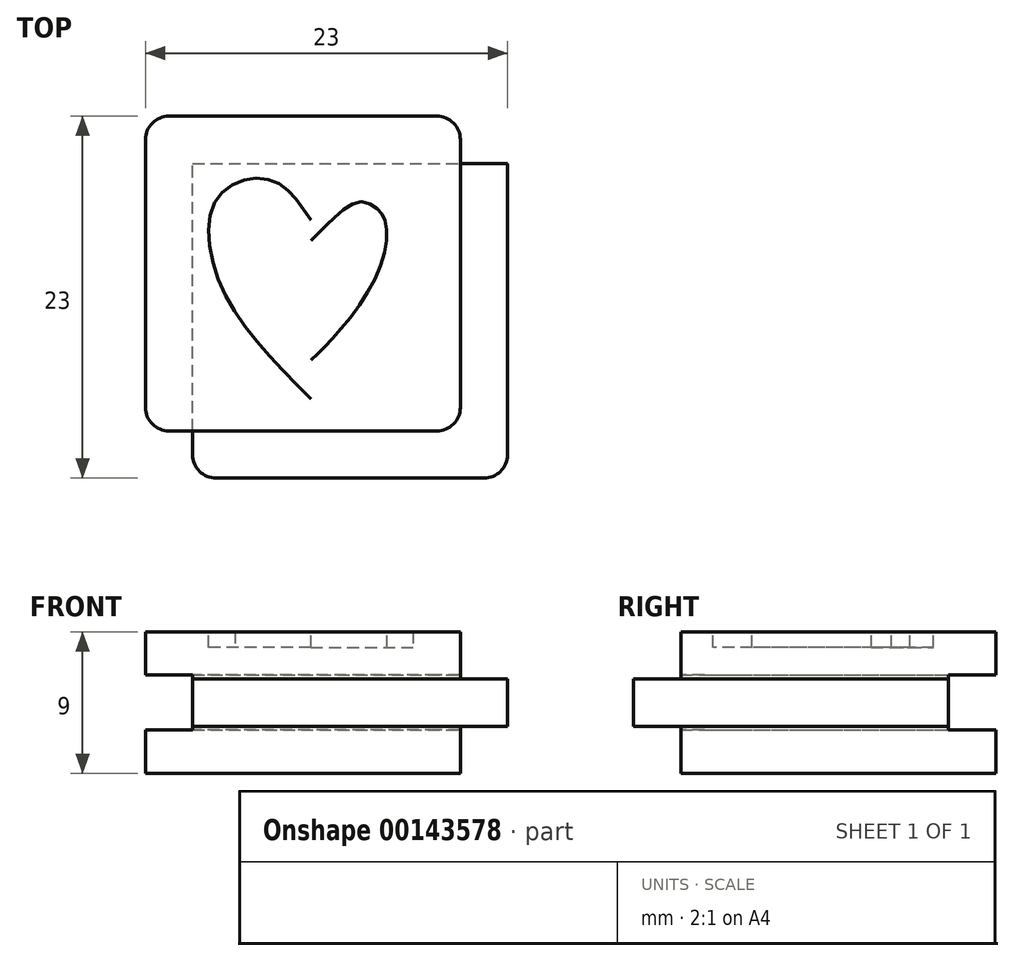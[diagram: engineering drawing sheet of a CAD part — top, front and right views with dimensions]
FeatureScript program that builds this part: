
annotation { "Feature Type Name" : "Feature", "Feature Type Description" : "" }
export const myFeature = defineFeature(function(context is Context, id is Id, definition is map)
    precondition{}
    {
        {
            var Q0;
            Q0=qCreatedBy(makeId("Front.planeOp"),FACE);
            var sketch = newSketch(context, id + "F0", { "sketchPlane" : qUnion([Q0])});
            skLineSegment(sketch, "E0.bottom", {"start": v(10, 4.5) * mm, "end": v(-10, 4.5) * mm});
            skLineSegment(sketch, "E0.top", {"start": v(10, -4.5) * mm, "end": v(-10, -4.5) * mm});
            skLineSegment(sketch, "E0.left", {"start": v(10, 4.5) * mm, "end": v(10, -4.5) * mm});
            skLineSegment(sketch, "E0.right", {"start": v(-10, 4.5) * mm, "end": v(-10, -4.5) * mm});
            skPoint(sketch, "E0.middle", {"position": v(0, 0) * mm});
            skLineSegment(sketch, "E1.bottom", {"start": v(13, 1.5) * mm, "end": v(7, 1.5) * mm});
            skLineSegment(sketch, "E1.top", {"start": v(13, -1.5) * mm, "end": v(7, -1.5) * mm});
            skLineSegment(sketch, "E1.left", {"start": v(13, 1.5) * mm, "end": v(13, -1.5) * mm});
            skLineSegment(sketch, "E1.right", {"start": v(7, 1.5) * mm, "end": v(7, -1.5) * mm});
            skPoint(sketch, "E1.middle", {"position": v(10, 0) * mm});
            skLineSegment(sketch, "E2.bottom", {"start": v(7, 1.5) * mm, "end": v(-7, 1.5) * mm});
            skLineSegment(sketch, "E2.top", {"start": v(7, -1.5) * mm, "end": v(-7, -1.5) * mm});
            skLineSegment(sketch, "E2.right", {"start": v(-7, 1.5) * mm, "end": v(-7, -1.5) * mm});
            skLineSegment(sketch, "E3.bottom", {"start": v(-7, -1.5) * mm, "end": v(-10, -1.5) * mm});
            skLineSegment(sketch, "E3.top", {"start": v(-7, 1.5) * mm, "end": v(-10, 1.5) * mm});
            skLineSegment(sketch, "E3.left", {"start": v(-7, -1.5) * mm, "end": v(-7, 1.5) * mm});
            skLineSegment(sketch, "E3.right", {"start": v(-10, -1.5) * mm, "end": v(-10, 1.5) * mm});
            skSolve(sketch);
        }
        {
            var Q0;
            {var subQ5=sQuery(id+"F0.wireOp",EDGE,"E0.bottom");Q0=makeQuery(id+"F0.imprint","IMPRINT",FACE,{"disambiguationData":[TD([[makeQuery(id+"F0.imprint","IMPRINT",EDGE,{"derivedFrom":subQ5}),1.0]])]});}
            var Q1;
            Q1=makeQuery(id+"F0.imprint","IMPRINT",FACE,{"disambiguationData":[TD([[makeQuery(id+"F0.imprint","IMPRINT",EDGE,{"derivedFrom":sQuery(id+"F0.wireOp",EDGE,"E2.bottom")}),1.0]])]});
            var Q2;
            {var subQ5=sQuery(id+"F0.wireOp",EDGE,"E1.left");Q2=makeQuery(id+"F0.imprint","IMPRINT",FACE,{"disambiguationData":[TD([[makeQuery(id+"F0.imprint","IMPRINT",EDGE,{"derivedFrom":subQ5}),-1.0]])]});}
            var Q3;
            {var subQ5=sQuery(id+"F0.wireOp",EDGE,"E1.right");Q3=makeQuery(id+"F0.imprint","IMPRINT",FACE,{"disambiguationData":[TD([[makeQuery(id+"F0.imprint","IMPRINT",EDGE,{"derivedFrom":subQ5}),1.0]])]});}
            var Q4;
            Q4=makeQuery(id+"F0.imprint","IMPRINT",FACE,{"disambiguationData":[TD([[makeQuery(id+"F0.imprint","IMPRINT",EDGE,{"derivedFrom":sQuery(id+"F0.wireOp",EDGE,"E3.bottom")}),-1.0]])]});
            var Q5;
            {var subQ5=sQuery(id+"F0.wireOp",EDGE,"E0.top");Q5=makeQuery(id+"F0.imprint","IMPRINT",FACE,{"disambiguationData":[TD([[makeQuery(id+"F0.imprint","IMPRINT",EDGE,{"derivedFrom":subQ5}),-1.0]])]});}
            extrude(context, id + "F1", {"entities" : qUnion([Q0, Q1, Q2, Q3, Q4, Q5]), "oppositeDirection" : true, "depth" : 20 * mm});
        }
        {
            var Q0;
            Q0=makeQuery(id+"F0.imprint","IMPRINT",FACE,{"disambiguationData":[TD([[makeQuery(id+"F0.imprint","IMPRINT",EDGE,{"derivedFrom":sQuery(id+"F0.wireOp",EDGE,"E3.bottom")}),-1.0]])]});
            var Q1;
            Q1=makeQuery(id+"F0.imprint","IMPRINT",FACE,{"disambiguationData":[TD([[makeQuery(id+"F0.imprint","IMPRINT",EDGE,{"derivedFrom":sQuery(id+"F0.wireOp",EDGE,"E2.bottom")}),1.0]])]});
            var Q2;
            {var subQ5=sQuery(id+"F0.wireOp",EDGE,"E1.right");Q2=makeQuery(id+"F0.imprint","IMPRINT",FACE,{"disambiguationData":[TD([[makeQuery(id+"F0.imprint","IMPRINT",EDGE,{"derivedFrom":subQ5}),1.0]])]});}
            var Q3;
            {var subQ5=sQuery(id+"F0.wireOp",EDGE,"E1.left");Q3=makeQuery(id+"F0.imprint","IMPRINT",FACE,{"disambiguationData":[TD([[makeQuery(id+"F0.imprint","IMPRINT",EDGE,{"derivedFrom":subQ5}),-1.0]])]});}
            extrude(context, id + "F2", {"entities" : qUnion([Q0, Q1, Q2, Q3]), "operationType" : NewBodyOperationType.ADD, "depth" : 3 * mm});
        }
        {
            var Q0;
            {var subQ0=sQuery(id+"F0.wireOp",EDGE,"E1.left");Q0=makeQuery(id+"F2.boolean.opBoolean","MERGE",FACE,{"derivedFrom":[makeQuery(id+"F1.opExtrude","SWEPT_FACE",FACE,{"disambiguationData":[OSD([subQ0])]}),makeQuery(id+"F2.opExtrude","SWEPT_FACE",FACE,{"disambiguationData":[OSD([subQ0])]})]});}
            var sketch = newSketch(context, id + "F3", { "sketchPlane" : qUnion([Q0])});
            skLineSegment(sketch, "E4.bottom", {"start": v(23, 1.75) * mm, "end": v(17, 1.75) * mm});
            skLineSegment(sketch, "E4.top", {"start": v(23, -1.75) * mm, "end": v(17, -1.75) * mm});
            skLineSegment(sketch, "E4.left", {"start": v(23, 1.75) * mm, "end": v(23, -1.75) * mm});
            skLineSegment(sketch, "E4.right", {"start": v(17, 1.75) * mm, "end": v(17, -1.75) * mm});
            skPoint(sketch, "E4.middle", {"position": v(20, 0) * mm});
            skSolve(sketch);
        }
        {
            var Q0;
            {var subQ1=sQuery(id+"F3.wireOp",EDGE,"E4.bottom");Q0=makeQuery(id+"F3.imprint","IMPRINT",FACE,{"disambiguationData":[TD([[makeQuery(id+"F3.imprint","IMPRINT",EDGE,{"derivedFrom":subQ1}),1.0]])]});}
            var Q1;
            {var subQ1=sQuery(id+"F0.wireOp",EDGE,"E1.left");var subQ8=makeQuery(id+"F1.opExtrude","CAP_EDGE",EDGE,{"disambiguationData":[OSD([subQ1])],"isStart":false});Q1=makeQuery(id+"F3.imprint","IMPRINT",FACE,{"disambiguationData":[TD([[makeQuery(id+"F3.imprint","IMPRINT",EDGE,{"derivedFrom":subQ8}),-1.0]])]});}
            extrude(context, id + "F4", {"entities" : qUnion([Q0, Q1]), "operationType" : NewBodyOperationType.REMOVE, "oppositeDirection" : true, "depth" : 100 * mm});
        }
        {
            var Q0;
            Q0=makeQuery(id+"F4.boolean.opBoolean","COPY",FACE,{"derivedFrom":makeQuery(id+"F4.opExtrude","SWEPT_FACE",FACE,{"disambiguationData":[OSD([sQuery(id+"F3.wireOp",EDGE,"E4.right")])]})});
            var sketch = newSketch(context, id + "F5", { "sketchPlane" : qUnion([Q0])});
            skLineSegment(sketch, "E5.bottom", {"start": v(13, 1.75) * mm, "end": v(7, 1.75) * mm});
            skLineSegment(sketch, "E5.top", {"start": v(13, -1.75) * mm, "end": v(7, -1.75) * mm});
            skLineSegment(sketch, "E5.left", {"start": v(13, 1.75) * mm, "end": v(13, -1.75) * mm});
            skLineSegment(sketch, "E5.right", {"start": v(7, 1.75) * mm, "end": v(7, -1.75) * mm});
            skPoint(sketch, "E5.middle", {"position": v(10, 0) * mm});
            skSolve(sketch);
        }
        {
            var Q0;
            {var subQ3=sQuery(id+"F5.wireOp",EDGE,"E5.left");Q0=makeQuery(id+"F5.imprint","IMPRINT",FACE,{"disambiguationData":[TD([[makeQuery(id+"F5.imprint","IMPRINT",EDGE,{"derivedFrom":subQ3}),-1.0]])]});}
            var Q1;
            {var subQ4=sQuery(id+"F5.wireOp",EDGE,"E5.right");Q1=makeQuery(id+"F5.imprint","IMPRINT",FACE,{"disambiguationData":[TD([[makeQuery(id+"F5.imprint","IMPRINT",EDGE,{"derivedFrom":subQ4}),1.0]])]});}
            extrude(context, id + "F6", {"entities" : qUnion([Q0, Q1]), "operationType" : NewBodyOperationType.REMOVE, "oppositeDirection" : true, "depth" : 100 * mm});
        }
        {
            var Q0;
            Q0=makeQuery(id+"F6.boolean.opBoolean","INTERSECT",EDGE,{"derivedFrom":[makeQuery(id+"F2.opExtrude","CAP_FACE",FACE,{"disambiguationData":[OSD([sQuery(id+"F0.wireOp",EDGE,"E1.bottom"),sQuery(id+"F0.wireOp",EDGE,"E1.top"),sQuery(id+"F0.wireOp",EDGE,"E1.left"),sQuery(id+"F0.wireOp",EDGE,"E2.bottom"),sQuery(id+"F0.wireOp",EDGE,"E2.top"),sQuery(id+"F0.wireOp",EDGE,"E3.bottom"),sQuery(id+"F0.wireOp",EDGE,"E3.top"),sQuery(id+"F0.wireOp",EDGE,"E3.right")])],"isStart":false}),makeQuery(id+"F6.opExtrude","SWEPT_FACE",FACE,{"disambiguationData":[OSD([sQuery(id+"F5.wireOp",EDGE,"E5.right")])]})]});
            var Q1;
            Q1=makeQuery(id+"F2.opExtrude","CAP_EDGE",EDGE,{"disambiguationData":[OSD([sQuery(id+"F0.wireOp",EDGE,"E1.left")])],"isStart":false});
            var Q2;
            {var subQ0=sQuery(id+"F0.wireOp",EDGE,"E0.left");Q2=makeQuery(id+"F1.opExtrude","CAP_EDGE",EDGE,{"disambiguationData":[OSD([subQ0]),TDD([makeQuery(id+"F0.imprint","IMPRINT",EDGE,{"disambiguationData":[TD([[makeQuery(id+"F0.imprint","INTERSECT",VERTEX,{"derivedFrom":[sQuery(id+"F0.wireOp",EDGE,"E0.bottom"),subQ0]}),-1.0]])],"derivedFrom":subQ0})])],"isStart":true});}
            var Q3;
            {var subQ0=sQuery(id+"F0.wireOp",EDGE,"E0.left");Q3=makeQuery(id+"F1.opExtrude","CAP_EDGE",EDGE,{"disambiguationData":[OSD([subQ0]),TDD([makeQuery(id+"F0.imprint","IMPRINT",EDGE,{"disambiguationData":[TD([[makeQuery(id+"F0.imprint","INTERSECT",VERTEX,{"derivedFrom":[sQuery(id+"F0.wireOp",EDGE,"E0.top"),subQ0]}),1.0]])],"derivedFrom":subQ0})])],"isStart":true});}
            var Q4;
            {var subQ0=sQuery(id+"F0.wireOp",EDGE,"E3.right");var subQ1=sQuery(id+"F0.wireOp",EDGE,"E0.right");var subQ3=sQuery(id+"F0.wireOp",EDGE,"E0.top");Q4=makeQuery(id+"F2.boolean.opBoolean","SPLIT",EDGE,{"disambiguationData":[TD([makeQuery(id+"F1.opExtrude","SWEPT_FACE",FACE,{"disambiguationData":[OSD([subQ3])]})])],"derivedFrom":makeQuery(id+"F1.opExtrude","CAP_EDGE",EDGE,{"disambiguationData":[OSD([subQ1,subQ0])],"isStart":true})});}
            var Q5;
            {var subQ1=sQuery(id+"F0.wireOp",EDGE,"E3.right");var subQ2=sQuery(id+"F0.wireOp",EDGE,"E0.right");var subQ3=sQuery(id+"F0.wireOp",EDGE,"E0.bottom");Q5=makeQuery(id+"F2.boolean.opBoolean","SPLIT",EDGE,{"disambiguationData":[TD([makeQuery(id+"F1.opExtrude","SWEPT_FACE",FACE,{"disambiguationData":[OSD([subQ3])]})])],"derivedFrom":makeQuery(id+"F1.opExtrude","CAP_EDGE",EDGE,{"disambiguationData":[OSD([subQ2,subQ1])],"isStart":true})});}
            var Q6;
            Q6=makeQuery(id+"F6.boolean.opBoolean","COPY",EDGE,{"derivedFrom":makeQuery(id+"F6.opExtrude","CAP_EDGE",EDGE,{"disambiguationData":[OSD([sQuery(id+"F5.wireOp",EDGE,"E5.right")])],"isStart":true})});
            var Q7;
            {var subQ0=sQuery(id+"F0.wireOp",EDGE,"E3.right");var subQ1=sQuery(id+"F0.wireOp",EDGE,"E0.right");var subQ2=sQuery(id+"F0.wireOp",EDGE,"E0.bottom");Q7=makeQuery(id+"F4.boolean.opBoolean","SPLIT",EDGE,{"disambiguationData":[TD([makeQuery(id+"F1.opExtrude","SWEPT_FACE",FACE,{"disambiguationData":[OSD([subQ2])]})])],"derivedFrom":makeQuery(id+"F1.opExtrude","CAP_EDGE",EDGE,{"disambiguationData":[OSD([subQ1,subQ0])],"isStart":false})});}
            var Q8;
            {var subQ0=sQuery(id+"F0.wireOp",EDGE,"E3.right");var subQ1=sQuery(id+"F0.wireOp",EDGE,"E0.right");var subQ2=sQuery(id+"F0.wireOp",EDGE,"E0.top");Q8=makeQuery(id+"F4.boolean.opBoolean","SPLIT",EDGE,{"disambiguationData":[TD([makeQuery(id+"F1.opExtrude","SWEPT_FACE",FACE,{"disambiguationData":[OSD([subQ2])]})])],"derivedFrom":makeQuery(id+"F1.opExtrude","CAP_EDGE",EDGE,{"disambiguationData":[OSD([subQ1,subQ0])],"isStart":false})});}
            var Q9;
            Q9=makeQuery(id+"F4.boolean.opBoolean","COPY",EDGE,{"derivedFrom":makeQuery(id+"F4.opExtrude","CAP_EDGE",EDGE,{"disambiguationData":[OSD([sQuery(id+"F3.wireOp",EDGE,"E4.right")])],"isStart":true})});
            var Q10;
            {var subQ0=sQuery(id+"F0.wireOp",EDGE,"E0.left");Q10=makeQuery(id+"F1.opExtrude","CAP_EDGE",EDGE,{"disambiguationData":[OSD([subQ0]),TDD([makeQuery(id+"F0.imprint","IMPRINT",EDGE,{"disambiguationData":[TD([[makeQuery(id+"F0.imprint","INTERSECT",VERTEX,{"derivedFrom":[sQuery(id+"F0.wireOp",EDGE,"E0.bottom"),subQ0]}),-1.0]])],"derivedFrom":subQ0})])],"isStart":false});}
            var Q11;
            {var subQ0=sQuery(id+"F0.wireOp",EDGE,"E0.left");Q11=makeQuery(id+"F1.opExtrude","CAP_EDGE",EDGE,{"disambiguationData":[OSD([subQ0]),TDD([makeQuery(id+"F0.imprint","IMPRINT",EDGE,{"disambiguationData":[TD([[makeQuery(id+"F0.imprint","INTERSECT",VERTEX,{"derivedFrom":[sQuery(id+"F0.wireOp",EDGE,"E0.top"),subQ0]}),1.0]])],"derivedFrom":subQ0})])],"isStart":false});}
            fillet(context, id + "F7", {"entities" : qUnion([Q0, Q1, Q2, Q3, Q4, Q5, Q6, Q7, Q8, Q9, Q10, Q11]), "radius" : 1.5 * mm, "tangentPropagation" : true, "allowEdgeOverflow" : false});
        }
        {
            var Q0;
            Q0=makeQuery(id+"F1.opExtrude","SWEPT_FACE",FACE,{"disambiguationData":[OSD([sQuery(id+"F0.wireOp",EDGE,"E0.bottom")])]});
            var sketch = newSketch(context, id + "F8", { "sketchPlane" : qUnion([Q0])});
            skLineSegment(sketch, "E6", {"start": v(0.5, 20) * mm, "end": v(0.5, 0) * mm});
            skFitSpline(sketch, "E7", {"points": [v(0.5, 13.4) * mm, v(-2.03, 15.93) * mm, v(-5.36, 14.89) * mm, v(-5.2, 9.23) * mm, v(0.5, 2.04) * mm], "startDerivative": vector(-10.35, 15.87) * mm, "endDerivative": vector(20.68, -20.66) * mm});
            skFitSpline(sketch, "E8", {"points": [v(0.5, 12.63) * mm, v(-1.66, 14.93) * mm, v(-3.18, 15.24) * mm, v(-4.68, 14.22) * mm, v(-5.03, 11.83) * mm, v(-3.22, 7.44) * mm, v(0.5, 3.22) * mm], "startDerivative": vector(-12.82, 16.22) * mm, "endDerivative": vector(17.89, -17.68) * mm});
            skFitSpline(sketch, "E9.MirrorCS", {"points": [v(0.5, 12.63) * mm, v(2.67, 14.93) * mm, v(4.2, 15.24) * mm, v(5.7, 14.22) * mm, v(6.05, 11.83) * mm, v(4.24, 7.44) * mm, v(0.5, 3.22) * mm], "startDerivative": vector(12.82, 16.22) * mm, "endDerivative": vector(-17.89, -17.68) * mm});
            skFitSpline(sketch, "E10.MirrorCS", {"points": [v(0.5, 13.4) * mm, v(3.04, 15.93) * mm, v(6.38, 14.89) * mm, v(6.22, 9.23) * mm, v(0.5, 2.04) * mm], "startDerivative": vector(10.35, 15.87) * mm, "endDerivative": vector(-20.68, -20.66) * mm});
            skFitSpline(sketch, "E11", {"points": [v(0.5, 12.1) * mm, v(-0.98, 13.55) * mm, v(-2.6, 14.56) * mm, v(-3.7, 14.11) * mm, v(-4.2, 13.4) * mm, v(-4.23, 11.57) * mm, v(-2.8, 8.35) * mm, v(-0.69, 5.68) * mm, v(0.5, 4.5) * mm], "startDerivative": vector(-11.13, 11.08) * mm, "endDerivative": vector(9.68, -9) * mm});
            skFitSpline(sketch, "E12.MirrorCS", {"points": [v(0.5, 12.1) * mm, v(2, 13.55) * mm, v(3.62, 14.56) * mm, v(4.7, 14.11) * mm, v(5.2, 13.4) * mm, v(5.25, 11.57) * mm, v(3.82, 8.35) * mm, v(1.7, 5.68) * mm, v(0.5, 4.5) * mm], "startDerivative": vector(11.13, 11.08) * mm, "endDerivative": vector(-9.68, -9) * mm});
            skSolve(sketch);
        }
        {
            var Q0;
            {var subQ1=sQuery(id+"F8.wireOp",EDGE,"E7");Q0=makeQuery(id+"F8.imprint","IMPRINT",FACE,{"disambiguationData":[TD([[makeQuery(id+"F8.imprint","IMPRINT",EDGE,{"derivedFrom":subQ1}),1.0]])]});}
            var Q1;
            {var subQ3=sQuery(id+"F8.wireOp",EDGE,"E9.MirrorCS");Q1=makeQuery(id+"F8.imprint","IMPRINT",FACE,{"disambiguationData":[TD([[makeQuery(id+"F8.imprint","IMPRINT",EDGE,{"derivedFrom":subQ3}),1.0]])]});}
            var Q2;
            {var subQ0=sQuery(id+"F8.wireOp",EDGE,"E9.MirrorCS");Q2=makeQuery(id+"F8.imprint","IMPRINT",FACE,{"disambiguationData":[TD([[makeQuery(id+"F8.imprint","IMPRINT",EDGE,{"derivedFrom":subQ0}),-1.0]])]});}
            var Q3;
            {var subQ1=sQuery(id+"F8.wireOp",EDGE,"E8");Q3=makeQuery(id+"F8.imprint","IMPRINT",FACE,{"disambiguationData":[TD([[makeQuery(id+"F8.imprint","IMPRINT",EDGE,{"derivedFrom":subQ1}),1.0]])]});}
            extrude(context, id + "F9", {"entities" : qUnion([Q0, Q1, Q2, Q3]), "operationType" : NewBodyOperationType.REMOVE, "oppositeDirection" : true, "depth" : 1 * mm});
        }
    });
